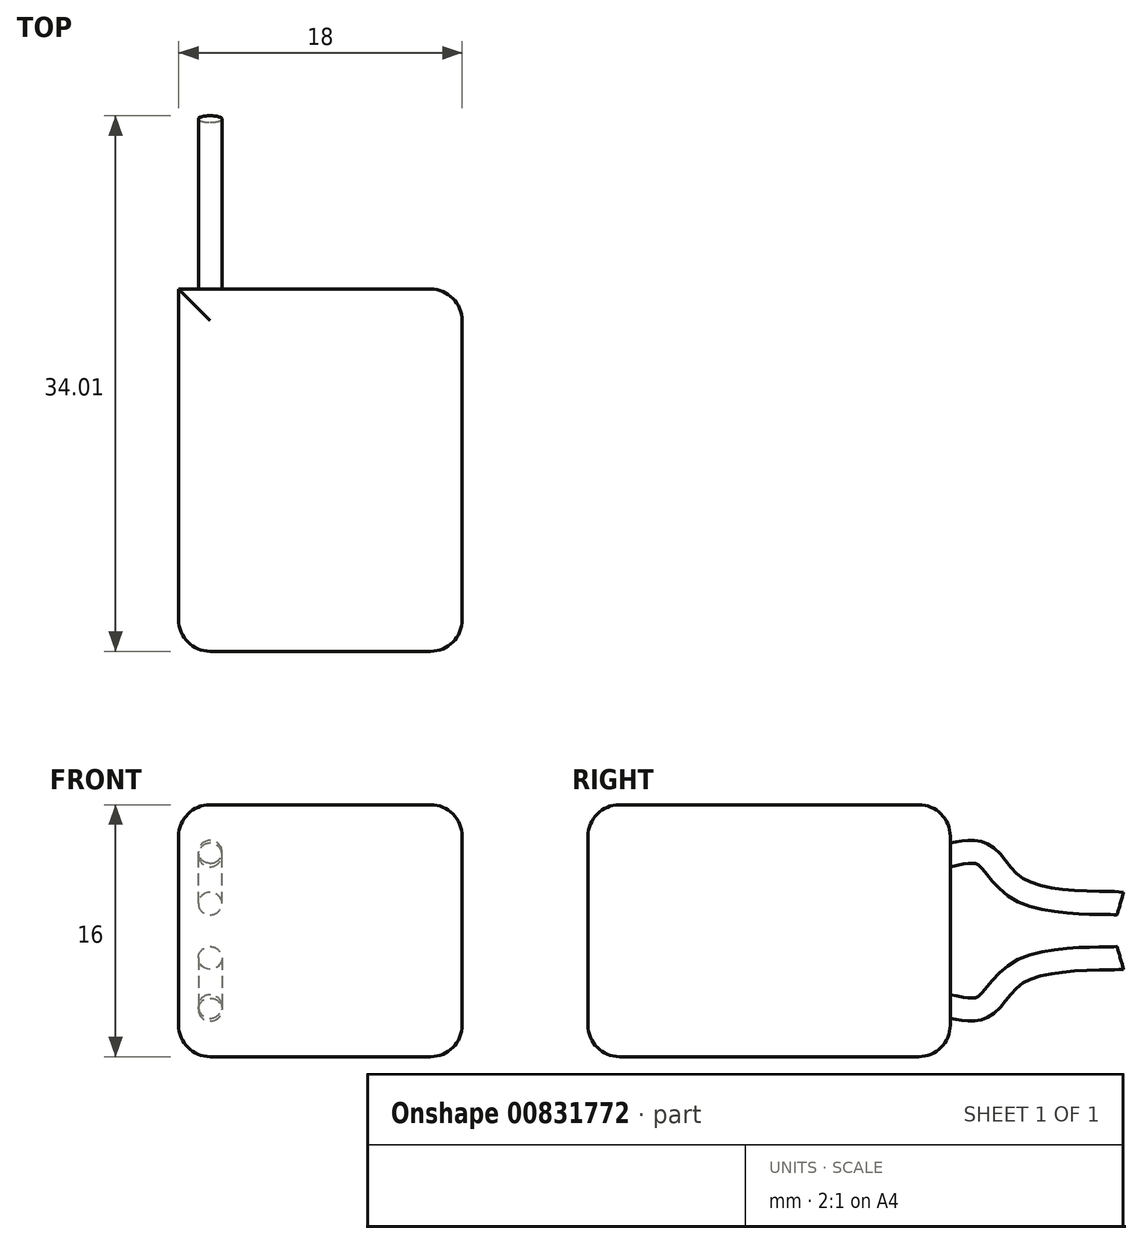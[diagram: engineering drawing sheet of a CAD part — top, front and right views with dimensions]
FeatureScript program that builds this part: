
annotation { "Feature Type Name" : "Feature", "Feature Type Description" : "" }
export const myFeature = defineFeature(function(context is Context, id is Id, definition is map)
    precondition{}
    {
        {
            var Q0;
            Q0=qCreatedBy(makeId("Top.planeOp"),FACE);
            var sketch = newSketch(context, id + "F0", { "sketchPlane" : qUnion([Q0])});
            skLineSegment(sketch, "E0.bottom", {"start": v(0, 0) * mm, "end": v(18, 0) * mm});
            skLineSegment(sketch, "E0.top", {"start": v(0, 23) * mm, "end": v(18, 23) * mm});
            skLineSegment(sketch, "E0.left", {"start": v(0, 0) * mm, "end": v(0, 23) * mm});
            skLineSegment(sketch, "E0.right", {"start": v(18, 0) * mm, "end": v(18, 23) * mm});
            skSolve(sketch);
        }
        {
            var Q0;
            Q0=makeQuery(id+"F0.imprint","IMPRINT",FACE,{"disambiguationData":[TD([[makeQuery(id+"F0.imprint","IMPRINT",EDGE,{"derivedFrom":sQuery(id+"F0.wireOp",EDGE,"E0.bottom")}),1.0]])]});
            extrude(context, id + "F1", {"entities" : qUnion([Q0]), "depth" : 16 * mm, "offsetDistance" : 25 * mm});
        }
        {
            var Q0;
            Q0=makeQuery(id+"F1.opExtrude","SWEPT_FACE",FACE,{"disambiguationData":[OSD([sQuery(id+"F0.wireOp",EDGE,"E0.top")])]});
            var sketch = newSketch(context, id + "F2", { "sketchPlane" : qUnion([Q0])});
            skCircle(sketch, "E1", {"center": v(-2, 3.19) * mm, "radius": 0.75 * mm});
            skSolve(sketch);
        }
        {
            var Q0;
            Q0=makeQuery(id+"F1.opExtrude","SWEPT_FACE",FACE,{"disambiguationData":[OSD([sQuery(id+"F0.wireOp",EDGE,"E0.left")])]});
            cPlane(context, id + "F3", {"entities" : qUnion([Q0]), "cplaneType" : CPlaneType.OFFSET, "offset" : 2 * mm, "oppositeDirection" : true, "width" : 150 * mm, "height" : 150 * mm});
        }
        {
            var Q0;
            Q0=qCreatedBy(id+"F3.planeOp",FACE);
            var sketch = newSketch(context, id + "F4", { "sketchPlane" : qUnion([Q0])});
            skFitSpline(sketch, "E2", {"points": [v(-23, 3.19) * mm, v(-25.13, 3.19) * mm, v(-27.4, 5.38) * mm, v(-32.95, 6.24) * mm, v(-33.8, 6.27) * mm], "startDerivative": vector(-10.4, -2.24) * mm, "endDerivative": vector(-4.25, 0.3) * mm});
            skSolve(sketch);
        }
        {
            var Q0;
            Q0=makeQuery(id+"F2.imprint","IMPRINT",FACE,{"disambiguationData":[TD([[makeQuery(id+"F2.imprint","IMPRINT",EDGE,{"derivedFrom":sQuery(id+"F2.wireOp",EDGE,"E1")}),1.0]])]});
            var Q1;
            Q1=sQuery(id+"F4.wireOp",EDGE,"E2");
            sweep(context, id + "F5", {"profiles" : qUnion([Q0]), "path" : qUnion([Q1])});
        }
        {
            var Q0;
            Q0=makeQuery(id+"F1.opExtrude","CAP_FACE",FACE,{"disambiguationData":[OSD([sQuery(id+"F0.wireOp",EDGE,"E0.bottom"),sQuery(id+"F0.wireOp",EDGE,"E0.top"),sQuery(id+"F0.wireOp",EDGE,"E0.left"),sQuery(id+"F0.wireOp",EDGE,"E0.right")])],"isStart":true});
            var Q1;
            Q1=makeQuery(id+"F1.opExtrude","CAP_FACE",FACE,{"disambiguationData":[OSD([sQuery(id+"F0.wireOp",EDGE,"E0.bottom"),sQuery(id+"F0.wireOp",EDGE,"E0.top"),sQuery(id+"F0.wireOp",EDGE,"E0.left"),sQuery(id+"F0.wireOp",EDGE,"E0.right")])],"isStart":false});
            cPlane(context, id + "F6", {"entities" : qUnion([Q0, Q1]), "cplaneType" : CPlaneType.MID_PLANE, "offset" : 25 * mm, "width" : 150 * mm, "height" : 150 * mm});
        }
        {
            var Q0;
            Q0=makeQuery(id+"F5.opSweep","SWEPT_BODY",BODY,{"disambiguationData":[OSD([sQuery(id+"F2.wireOp",EDGE,"E1"),sQuery(id+"F4.wireOp",EDGE,"E2")])]});
            var Q1;
            Q1=qCreatedBy(id+"F6.planeOp",FACE);
            mirror(context, id + "F7", {"operationType" : NewBodyOperationType.ADD, "entities" : qUnion([Q0]), "mirrorPlane" : qUnion([Q1])});
        }
        {
            var Q0;
            Q0=makeQuery(id+"F1.opExtrude","CAP_EDGE",EDGE,{"disambiguationData":[OSD([sQuery(id+"F0.wireOp",EDGE,"E0.left")])],"isStart":false});
            var Q1;
            Q1=makeQuery(id+"F1.opExtrude","CAP_EDGE",EDGE,{"disambiguationData":[OSD([sQuery(id+"F0.wireOp",EDGE,"E0.left")])],"isStart":true});
            var Q2;
            Q2=makeQuery(id+"F1.opExtrude","CAP_EDGE",EDGE,{"disambiguationData":[OSD([sQuery(id+"F0.wireOp",EDGE,"E0.right")])],"isStart":true});
            var Q3;
            Q3=makeQuery(id+"F1.opExtrude","SWEPT_EDGE",EDGE,{"disambiguationData":[OSD([sQuery(id+"F0.wireOp",EDGE,"E0.bottom"),sQuery(id+"F0.wireOp",EDGE,"E0.right")])]});
            var Q4;
            Q4=makeQuery(id+"F1.opExtrude","CAP_EDGE",EDGE,{"disambiguationData":[OSD([sQuery(id+"F0.wireOp",EDGE,"E0.bottom")])],"isStart":true});
            var Q5;
            Q5=makeQuery(id+"F1.opExtrude","CAP_EDGE",EDGE,{"disambiguationData":[OSD([sQuery(id+"F0.wireOp",EDGE,"E0.bottom")])],"isStart":false});
            var Q6;
            Q6=makeQuery(id+"F1.opExtrude","SWEPT_EDGE",EDGE,{"disambiguationData":[OSD([sQuery(id+"F0.wireOp",EDGE,"E0.bottom"),sQuery(id+"F0.wireOp",EDGE,"E0.left")])]});
            var Q7;
            Q7=makeQuery(id+"F1.opExtrude","CAP_EDGE",EDGE,{"disambiguationData":[OSD([sQuery(id+"F0.wireOp",EDGE,"E0.top")])],"isStart":false});
            var Q8;
            Q8=makeQuery(id+"F1.opExtrude","SWEPT_EDGE",EDGE,{"disambiguationData":[OSD([sQuery(id+"F0.wireOp",EDGE,"E0.top"),sQuery(id+"F0.wireOp",EDGE,"E0.right")])]});
            var Q9;
            Q9=makeQuery(id+"F1.opExtrude","CAP_EDGE",EDGE,{"disambiguationData":[OSD([sQuery(id+"F0.wireOp",EDGE,"E0.top")])],"isStart":true});
            var Q10;
            Q10=makeQuery(id+"F1.opExtrude","CAP_EDGE",EDGE,{"disambiguationData":[OSD([sQuery(id+"F0.wireOp",EDGE,"E0.right")])],"isStart":false});
            fillet(context, id + "F8", {"entities" : qUnion([Q0, Q1, Q2, Q3, Q4, Q5, Q6, Q7, Q8, Q9, Q10]), "radius" : 2 * mm, "tangentPropagation" : true, "allowEdgeOverflow" : false});
        }
    });
